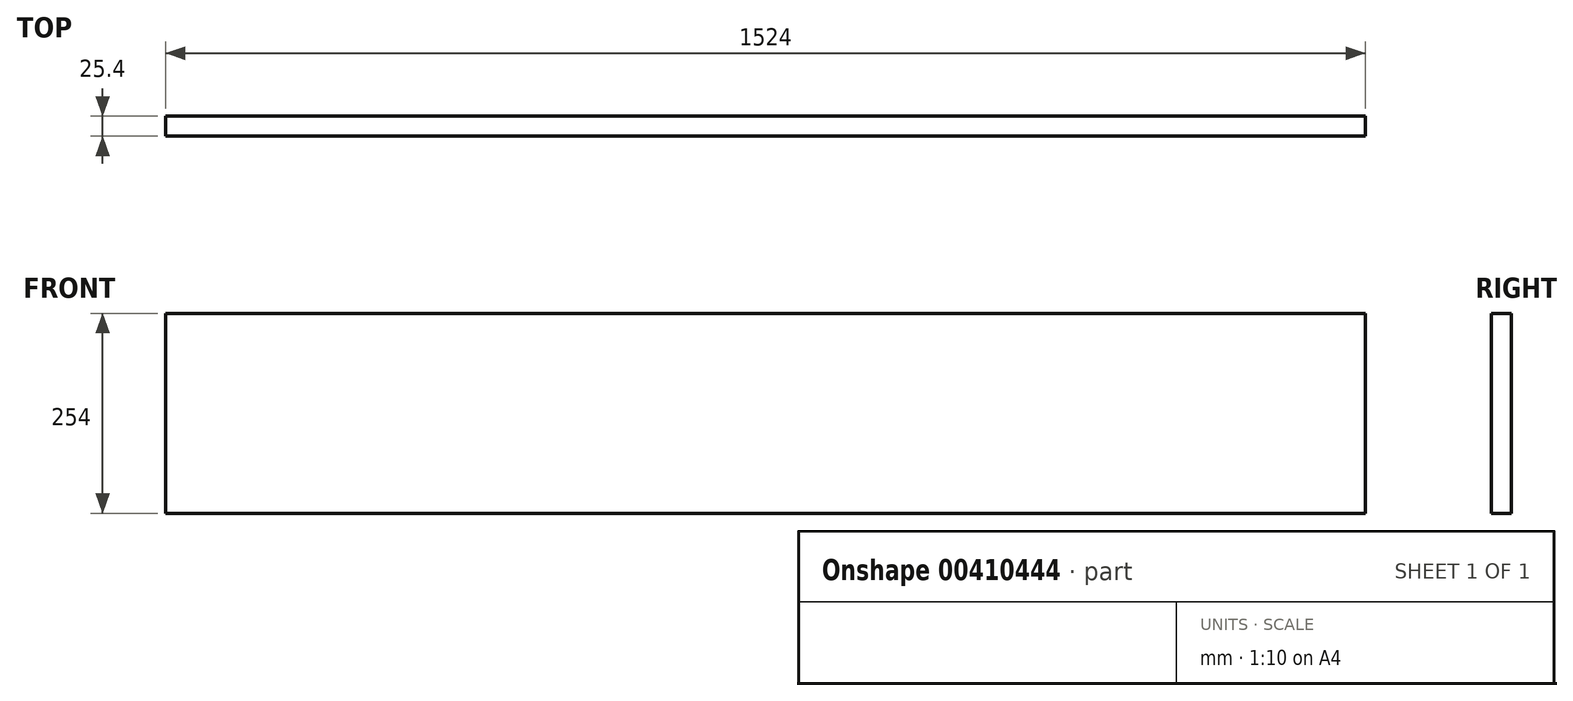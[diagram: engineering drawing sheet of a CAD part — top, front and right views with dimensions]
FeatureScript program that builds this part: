
annotation { "Feature Type Name" : "Feature", "Feature Type Description" : "" }
export const myFeature = defineFeature(function(context is Context, id is Id, definition is map)
    precondition{}
    {
        {
            var Q0;
            Q0=qCreatedBy(makeId("Front.planeOp"),FACE);
            var sketch = newSketch(context, id + "F0", { "sketchPlane" : qUnion([Q0])});
            skLineSegment(sketch, "E0.bottom", {"start": v(-762, 127) * mm, "end": v(762, 127) * mm});
            skLineSegment(sketch, "E0.top", {"start": v(-762, -127) * mm, "end": v(762, -127) * mm});
            skLineSegment(sketch, "E0.left", {"start": v(-762, 127) * mm, "end": v(-762, -127) * mm});
            skLineSegment(sketch, "E0.right", {"start": v(762, 127) * mm, "end": v(762, -127) * mm});
            skPoint(sketch, "E0.middle", {"position": v(0, 0) * mm});
            skSolve(sketch);
        }
        {
            var Q0;
            Q0=qSketchRegion(id+"F0",true);
            extrude(context, id + "F1", {"entities" : qUnion([Q0]), "depth" : 25.4 * mm, "offsetDistance" : 25.4 * mm});
        }
    });
